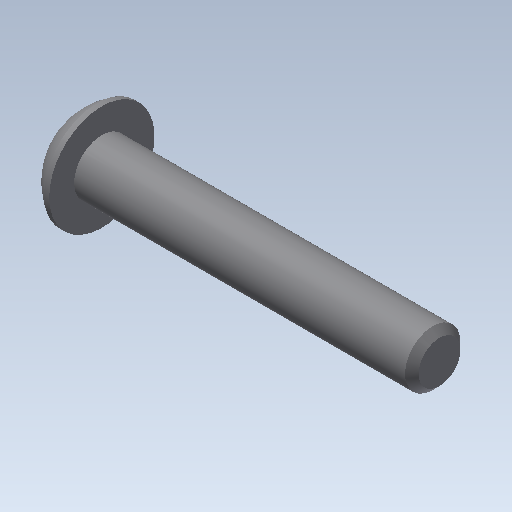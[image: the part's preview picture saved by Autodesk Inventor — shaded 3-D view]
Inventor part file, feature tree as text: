
AUTODESK INVENTOR PART (.ipt)
format: ipt  version: 2020 (Build 240168000, 168)  size: 136,192 bytes
history: native  units: in
note: dims shown in document units (in); Inventor stores cm internally (conversion verified against a paired STEP export)
features: other x2, extrude x1, chamfer x1, imported_body x1, sketch x1
ambient origin geometry x8: Origin, YZ Plane, XZ Plane, XY Plane, X Axis, Y Axis, Z Axis, Center Point
bodies: Body1 (feature_tree)
feature tree (6):
  parser-record x1  (decoder bookkeeping rows leaked as tree rows — omitted from the tree; the rows remain in map.json)
  other  "Bolt"
  extrude  "thread length"  Depth=1.0in TaperAngle=0.0deg
  chamfer  "thread chamfer"  Distance=0.02in Angle=45.0deg
  imported_body  "Base1"
  sketch  "Sketch1"  dims[d0=0.164in d1=1.0in d2=0.0in d3=0.02in d4=0.125in d5=45.0deg d7=0.0in d9=0.0in]
